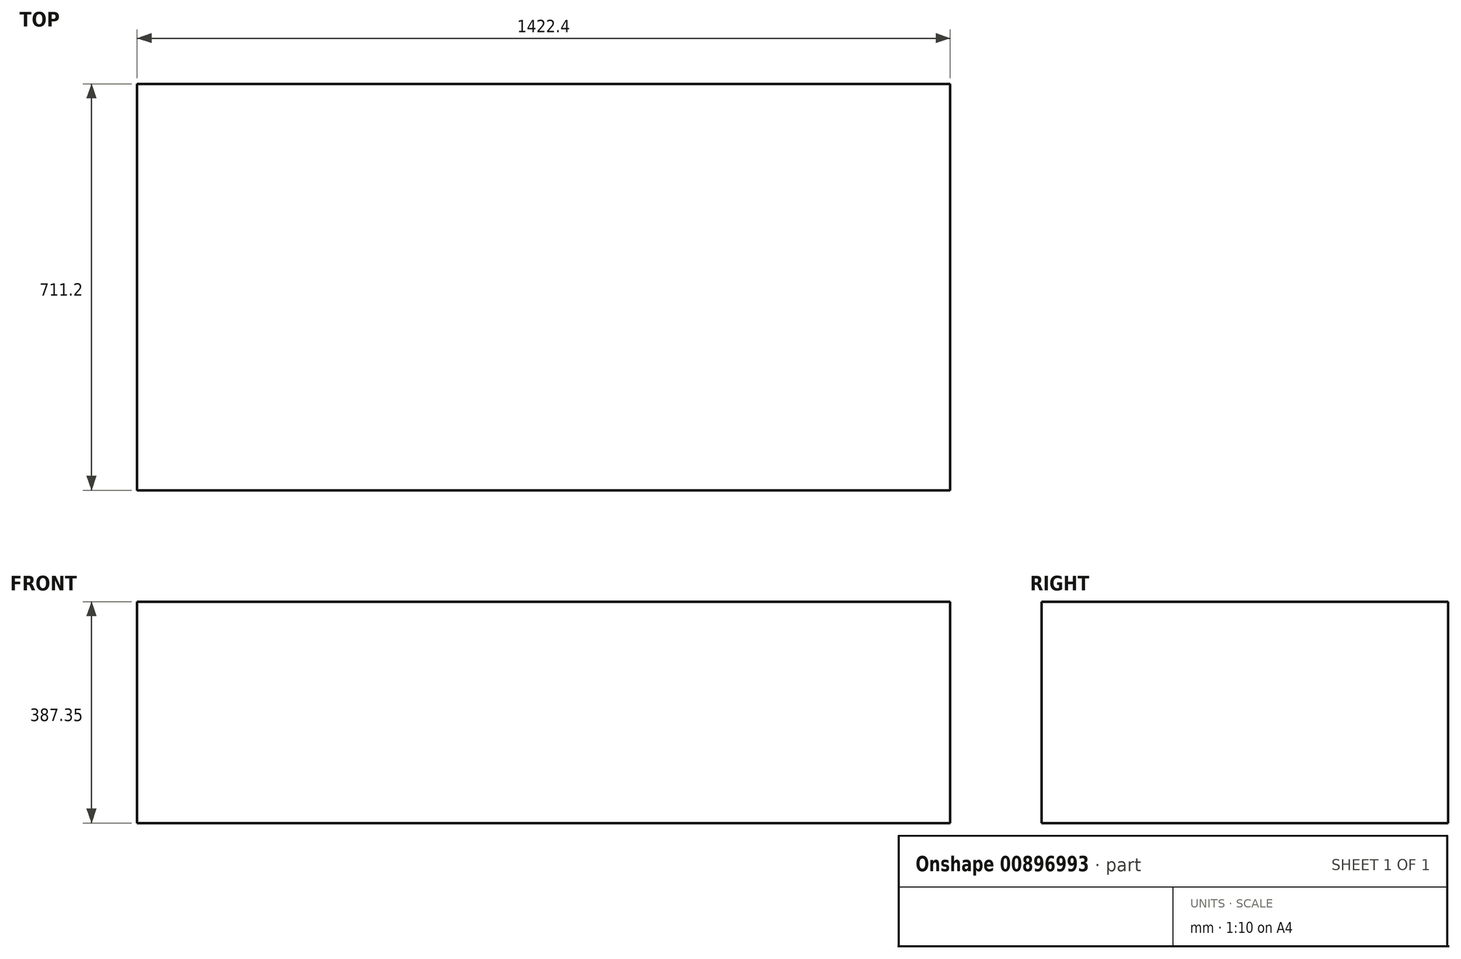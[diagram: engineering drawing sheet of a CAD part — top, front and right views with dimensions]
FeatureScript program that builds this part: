
annotation { "Feature Type Name" : "Feature", "Feature Type Description" : "" }
export const myFeature = defineFeature(function(context is Context, id is Id, definition is map)
    precondition{}
    {
        {
            var Q0;
            Q0=qCreatedBy(makeId("Top.planeOp"),FACE);
            var sketch = newSketch(context, id + "F0", { "sketchPlane" : qUnion([Q0])});
            skLineSegment(sketch, "E0.bottom", {"start": v(0, 0) * mm, "end": v(1422.4, 0) * mm});
            skLineSegment(sketch, "E0.top", {"start": v(0, 711.2) * mm, "end": v(1422.4, 711.2) * mm});
            skLineSegment(sketch, "E0.left", {"start": v(0, 0) * mm, "end": v(0, 711.2) * mm});
            skLineSegment(sketch, "E0.right", {"start": v(1422.4, 0) * mm, "end": v(1422.4, 711.2) * mm});
            skSolve(sketch);
        }
        {
            var Q0;
            Q0 = qSketchRegion(id + "F0", true);
            extrude(context, id + "F1", {"entities" : qUnion([Q0]), "depth" : 387.35 * mm, "offsetDistance" : 25.4 * mm});
        }
    });
